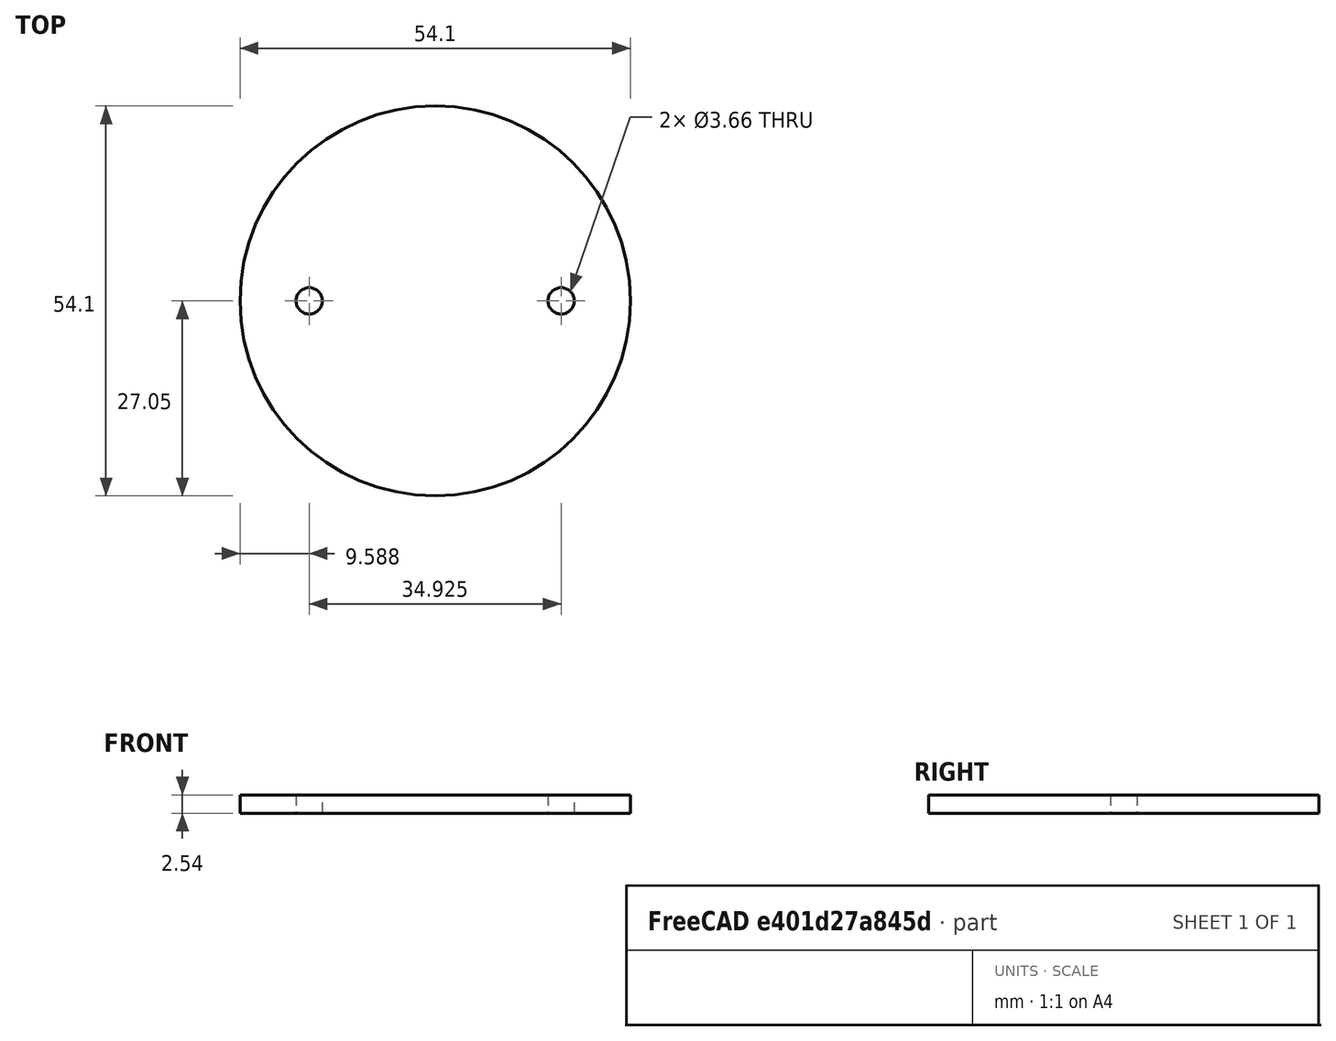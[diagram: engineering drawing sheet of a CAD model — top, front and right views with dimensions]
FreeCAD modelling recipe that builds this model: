
FCSTD DOCUMENT  (FreeCAD 0.19R24291 (Git))
Label: david base small holes
License: Creative Commons Attribution-ShareAlike
LicenseURL: http://creativecommons.org/licenses/by-sa/4.0/
objects: Sketcher::SketchObject×1, PartDesign::Pad×1, PartDesign::Body×1
note: 4 computed .brp shape members not serialized (recipe doc carries the construction recipe); baked Part::Feature solids carry a one-line shape summary decoded from their .brp

FEATURE [Sketcher::SketchObject] Sketch
  FullyConstrained = true
  MapMode = 5
  Support = -> [XY_Plane]
  sketch-geometry (8):
    g0: Circle CenterX=0 CenterY=0 CenterZ=0 NormalX=0 NormalY=0 NormalZ=1 AngleXU=0 Radius=27.051
    g1: Circle CenterX=-17.4625 CenterY=0 CenterZ=0 NormalX=0 NormalY=0 NormalZ=1 AngleXU=0 Radius=3.4925
    g2: Circle CenterX=17.4625 CenterY=0 CenterZ=0 NormalX=0 NormalY=0 NormalZ=1 AngleXU=0 Radius=3.4925
    g3: LineSegment StartX=-27.051 StartY=0 StartZ=0 EndX=-20.955 EndY=0 EndZ=0
    g4: LineSegment StartX=20.955 StartY=0 StartZ=0 EndX=27.051 EndY=0 EndZ=0
    g5: LineSegment StartX=-13.97 StartY=0 StartZ=0 EndX=13.97 EndY=0 EndZ=0
    g6: Circle CenterX=-17.4625 CenterY=0 CenterZ=0 NormalX=0 NormalY=0 NormalZ=1 AngleXU=0 Radius=1.8288
    g7: Circle CenterX=17.4625 CenterY=0 CenterZ=0 NormalX=0 NormalY=0 NormalZ=1 AngleXU=0 Radius=1.8288
  constraints (21):
    c: Coincident(g0,g-1)
    c: PointOnObject(g1,g-1)
    c: PointOnObject(g2,g-1)
    c: Equal(g1,g2)
    c: Diameter(g0) = 54.102
    c: PointOnObject(g3,g0)
    c: PointOnObject(g3,g1)
    c: PointOnObject(g4,g2)
    c: PointOnObject(g4,g0)
    c: Tangent(g4,g-1)
    c: Tangent(g3,g-1)
    c: Equal(g4,g3)
    c: PointOnObject(g5,g1)
    c: PointOnObject(g5,g2)
    c: Tangent(g-1,g5)
    c: DistanceX(g5,g5) = 27.94
    c: DistanceX(g3,g4) = 41.91
    c: Coincident(g6,g1)
    c: Coincident(g7,g2)
    c: Equal(g6,g7)
    c: Diameter(g6) = 3.6576
FEATURE [PartDesign::Pad] Pad
  Direction = (1,1,1)
  Length = 2.54
  Length2 = 99.9998
  Profile = -> Sketch
  Type = 0
FEATURE [PartDesign::Body] Body
  Group = -> [Sketch,Pad]
  Origin = -> Origin
  Tip = -> Pad
